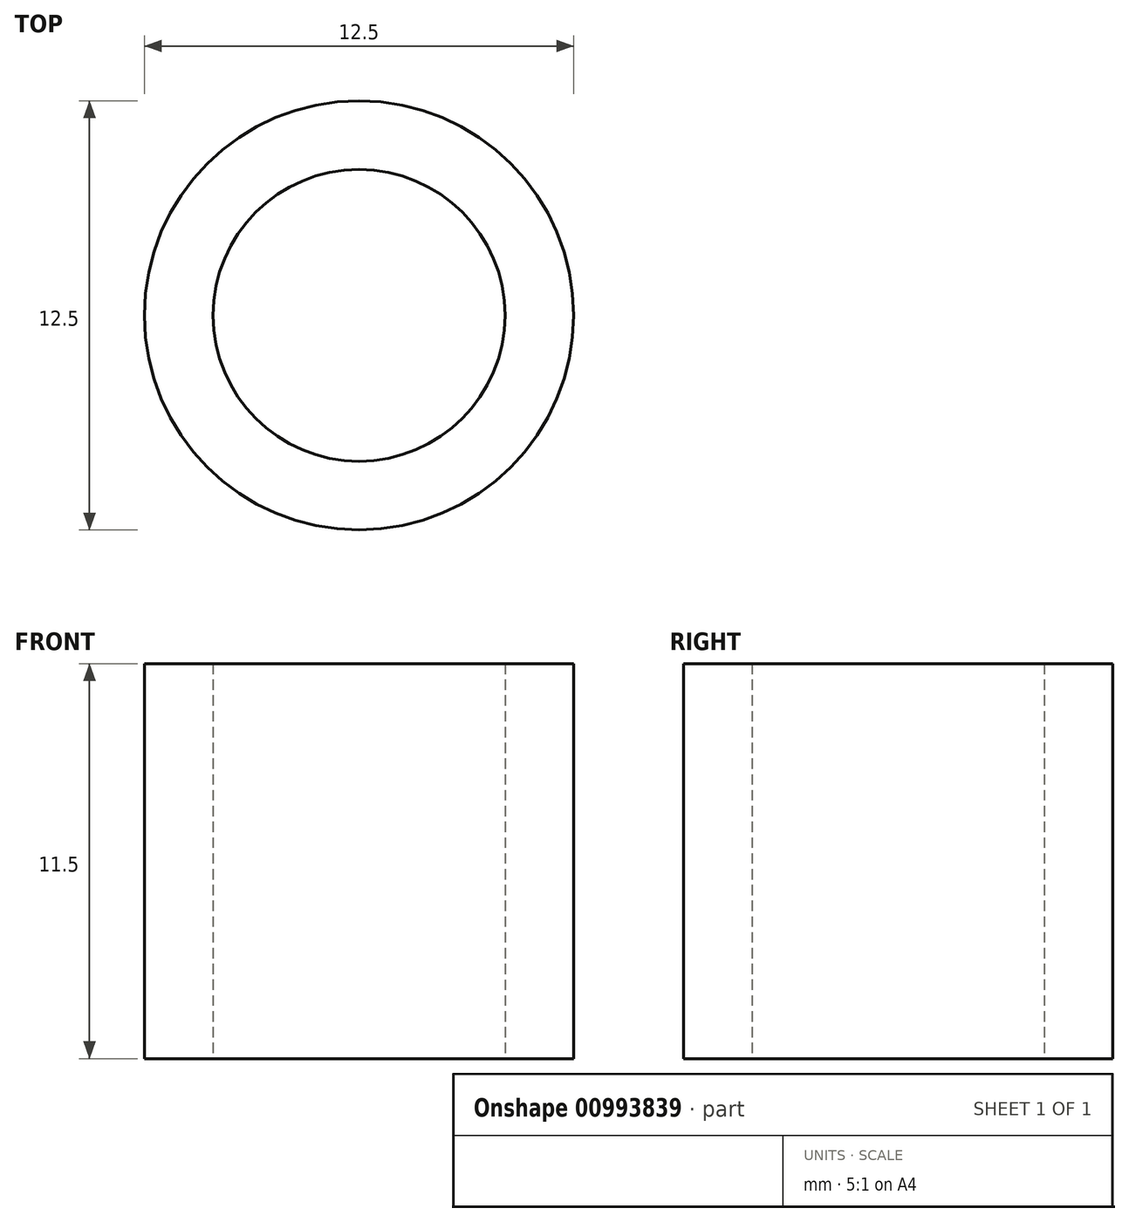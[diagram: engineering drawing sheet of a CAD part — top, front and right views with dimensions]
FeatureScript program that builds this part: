
annotation { "Feature Type Name" : "Feature", "Feature Type Description" : "" }
export const myFeature = defineFeature(function(context is Context, id is Id, definition is map)
    precondition{}
    {
        {
            var Q0;
            Q0=qCreatedBy(makeId("Top.planeOp"),FACE);
            var sketch = newSketch(context, id + "F0", { "sketchPlane" : qUnion([Q0])});
            skCircle(sketch, "E0", {"center": v(0, 0) * mm, "radius": 4.25 * mm});
            skCircle(sketch, "E1", {"center": v(0, 0) * mm, "radius": 6.25 * mm});
            skSolve(sketch);
        }
        {
            var Q0;
            Q0 = qSketchRegion(id + "F0", true);
            extrude(context, id + "F1", {"entities" : qUnion([Q0]), "depth" : 11.5 * mm, "offsetDistance" : 25 * mm});
        }
    });
